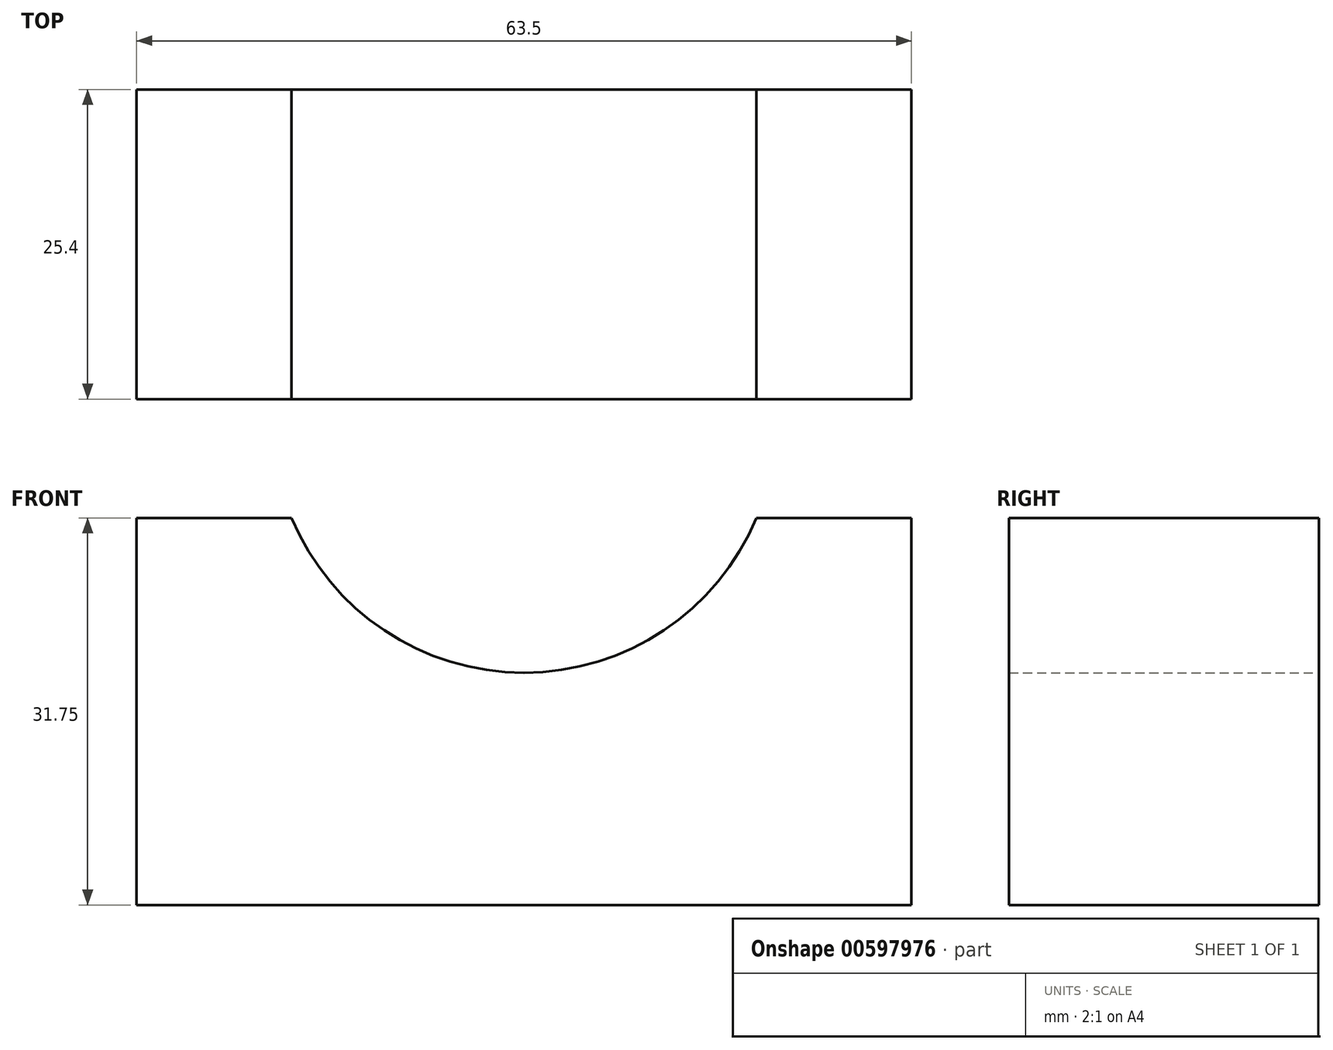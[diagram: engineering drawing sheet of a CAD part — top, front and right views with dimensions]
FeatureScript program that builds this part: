
annotation { "Feature Type Name" : "Feature", "Feature Type Description" : "" }
export const myFeature = defineFeature(function(context is Context, id is Id, definition is map)
    precondition{}
    {
        {
            var Q0;
            Q0=qCreatedBy(makeId("Front.planeOp"),FACE);
            var sketch = newSketch(context, id + "F0", { "sketchPlane" : qUnion([Q0])});
            skLineSegment(sketch, "E0", {"start": v(-63.5, 0) * mm, "end": v(-63.5, 31.75) * mm});
            skLineSegment(sketch, "E1", {"start": v(-63.5, 31.75) * mm, "end": v(-50.8, 31.75) * mm});
            skLineSegment(sketch, "E2", {"start": v(-63.5, 0) * mm, "end": v(0, 0) * mm});
            skLineSegment(sketch, "E3", {"start": v(0, 0) * mm, "end": v(0, 31.75) * mm});
            skLineSegment(sketch, "E4", {"start": v(0, 31.75) * mm, "end": v(-12.7, 31.75) * mm});
            skArc(sketch, "E5", {"start": v(-50.8, 31.75) * mm, "mid": v(-31.75, 19.05) * mm, "end": v(-12.7, 31.75) * mm});
            skSolve(sketch);
        }
        {
            var Q0;
            Q0=makeQuery(id+"F0.imprint","IMPRINT",FACE,{"disambiguationData":[TD([[makeQuery(id+"F0.imprint","IMPRINT",EDGE,{"derivedFrom":sQuery(id+"F0.wireOp",EDGE,"E0")}),-1.0]])]});
            extrude(context, id + "F1", {"entities" : qUnion([Q0]), "depth" : 25.4 * mm, "offsetDistance" : 25.4 * mm});
        }
    });
